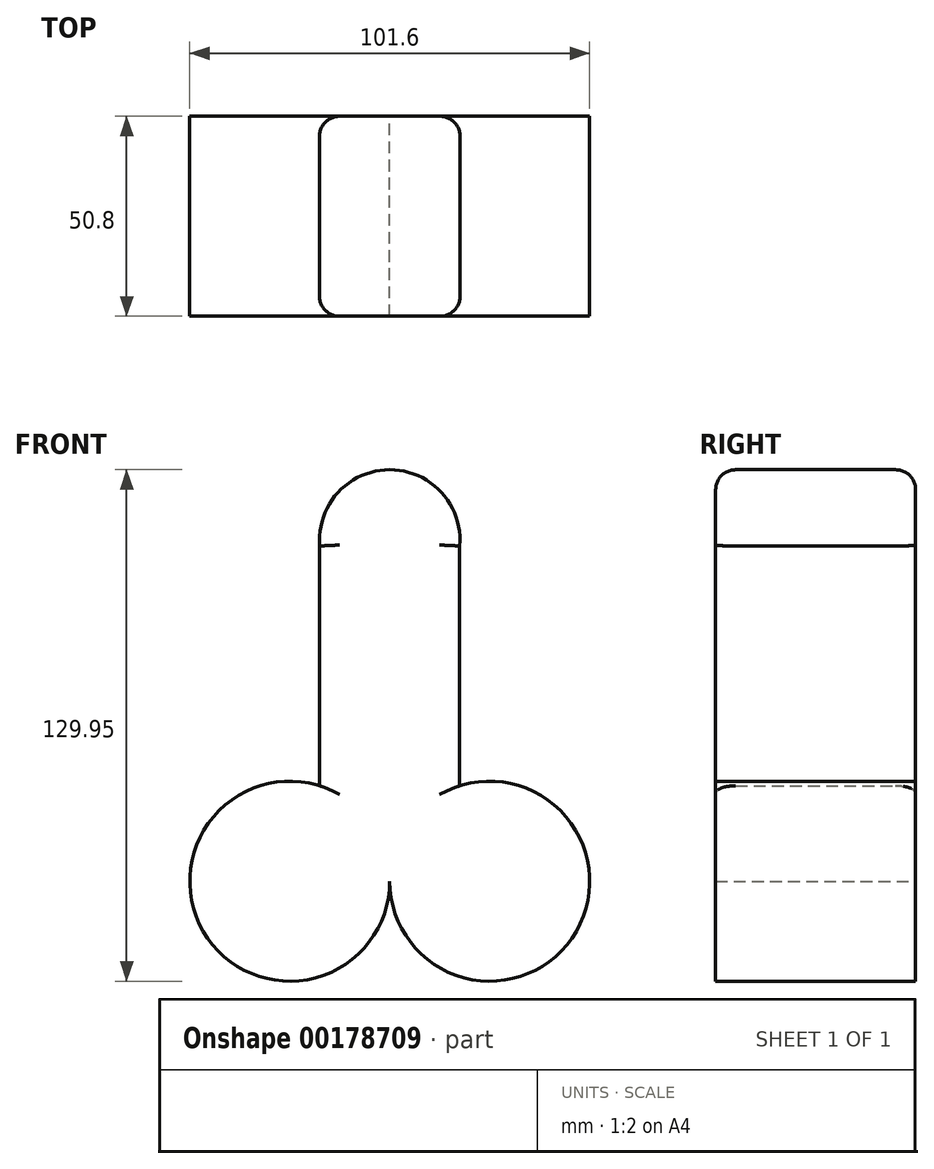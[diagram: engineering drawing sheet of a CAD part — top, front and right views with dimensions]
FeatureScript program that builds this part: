
annotation { "Feature Type Name" : "Feature", "Feature Type Description" : "" }
export const myFeature = defineFeature(function(context is Context, id is Id, definition is map)
    precondition{}
    {
        {
            var Q0;
            Q0=qCreatedBy(makeId("Front.planeOp"),FACE);
            var sketch = newSketch(context, id + "F0", { "sketchPlane" : qUnion([Q0])});
            skLineSegment(sketch, "E0", {"start": v(0, 0) * mm, "end": v(0, -36.83) * mm});
            skLineSegment(sketch, "E1", {"start": v(0, -36.83) * mm, "end": v(-25.4, -36.83) * mm});
            skCircle(sketch, "E2", {"center": v(-25.4, -36.83) * mm, "radius": 25.4 * mm});
            skLineSegment(sketch, "E3", {"start": v(0, -36.83) * mm, "end": v(25.4, -36.83) * mm});
            skCircle(sketch, "E4", {"center": v(25.4, -36.83) * mm, "radius": 25.4 * mm});
            skLineSegment(sketch, "E5", {"start": v(-25.4, -36.83) * mm, "end": v(-25.4, -11.43) * mm});
            skLineSegment(sketch, "E6", {"start": v(-25.4, -11.43) * mm, "end": v(-17.78, -11.43) * mm});
            skLineSegment(sketch, "E7", {"start": v(-17.78, -11.43) * mm, "end": v(-17.78, -12.6) * mm});
            skLineSegment(sketch, "E8", {"start": v(-17.78, -12.6) * mm, "end": v(-17.78, 48.36) * mm});
            skLineSegment(sketch, "E9", {"start": v(25.4, -36.83) * mm, "end": v(25.4, -11.43) * mm});
            skLineSegment(sketch, "E10", {"start": v(25.4, -11.43) * mm, "end": v(17.78, -11.43) * mm});
            skLineSegment(sketch, "E11", {"start": v(17.78, -11.43) * mm, "end": v(17.78, -12.6) * mm});
            skLineSegment(sketch, "E12", {"start": v(17.78, -12.6) * mm, "end": v(17.78, 48.36) * mm});
            skArc(sketch, "E13", {"start": v(17.78, 48.36) * mm, "mid": v(0, 67.72) * mm, "end": v(-17.78, 48.36) * mm});
            skSolve(sketch);
        }
        {
            var Q0;
            {var subQ0=sQuery(id+"F0.wireOp",EDGE,"E1");Q0=makeQuery(id+"F0.imprint","IMPRINT",FACE,{"disambiguationData":[TD([[makeQuery(id+"F0.imprint","IMPRINT",EDGE,{"derivedFrom":subQ0}),1.0]])]});}
            var Q1;
            {var subQ2=sQuery(id+"F0.wireOp",EDGE,"E13");Q1=makeQuery(id+"F0.imprint","IMPRINT",FACE,{"disambiguationData":[TD([[makeQuery(id+"F0.imprint","IMPRINT",EDGE,{"derivedFrom":subQ2}),1.0]])]});}
            var Q2;
            {var subQ0=sQuery(id+"F0.wireOp",EDGE,"E3");Q2=makeQuery(id+"F0.imprint","IMPRINT",FACE,{"disambiguationData":[TD([[makeQuery(id+"F0.imprint","IMPRINT",EDGE,{"derivedFrom":subQ0}),-1.0]])]});}
            var Q3;
            {var subQ0=sQuery(id+"F0.wireOp",EDGE,"E1");Q3=makeQuery(id+"F0.imprint","IMPRINT",FACE,{"disambiguationData":[TD([[makeQuery(id+"F0.imprint","IMPRINT",EDGE,{"derivedFrom":subQ0}),-1.0]])]});}
            var Q4;
            {var subQ0=sQuery(id+"F0.wireOp",EDGE,"E3");Q4=makeQuery(id+"F0.imprint","IMPRINT",FACE,{"disambiguationData":[TD([[makeQuery(id+"F0.imprint","IMPRINT",EDGE,{"derivedFrom":subQ0}),1.0]])]});}
            extrude(context, id + "F1", {"entities" : qUnion([Q0, Q1, Q2, Q3, Q4]), "depth" : 25.4 * mm, "hasSecondDirection" : true, "secondDirectionOppositeDirection" : true, "secondDirectionDepth" : 25.4 * mm});
        }
        {
            var Q0;
            Q0=makeQuery(id+"F1.opExtrude","CAP_EDGE",EDGE,{"disambiguationData":[OSD([sQuery(id+"F0.wireOp",EDGE,"E13")])],"isStart":false});
            var Q1;
            Q1=makeQuery(id+"F1.opExtrude","CAP_EDGE",EDGE,{"disambiguationData":[OSD([sQuery(id+"F0.wireOp",EDGE,"E8")])],"isStart":false});
            var Q2;
            Q2=makeQuery(id+"F1.opExtrude","CAP_EDGE",EDGE,{"disambiguationData":[OSD([sQuery(id+"F0.wireOp",EDGE,"E13")])],"isStart":true});
            fillet(context, id + "F2", {"entities" : qUnion([Q0, Q1, Q2]), "radius" : 5.08 * mm, "tangentPropagation" : true, "allowEdgeOverflow" : false});
        }
    });
